AUTODESK INVENTOR PART (.ipt)
format: ipt  version: 2024 (Build 280153000, 153)  size: 95,232 bytes
history: native  units: in
note: dims shown in document units (in); Inventor stores cm internally (conversion verified against a paired STEP export)
features: extrude x1, sketch x1
ambient origin geometry x8: Origin, YZ Plane, XZ Plane, XY Plane, X Axis, Y Axis, Z Axis, Center Point
bodies: Solid1 (feature_tree)
feature tree (2):
  extrude  "Extrusion1"  Depth=3.937in
  sketch  "Sketch2"  dims[d0=34.4488in d1=3.937in d9=0.315in d10=0.315in d11=0.315in d12=0.315in d13=0.315in d14=0.315in d15=5.9055in d16=1.9685in d17=5.9055in d18=5.9055in d19=6.8898in d20=5.9055in d21=1.9685in d22=0.748in d23=0.0in]
